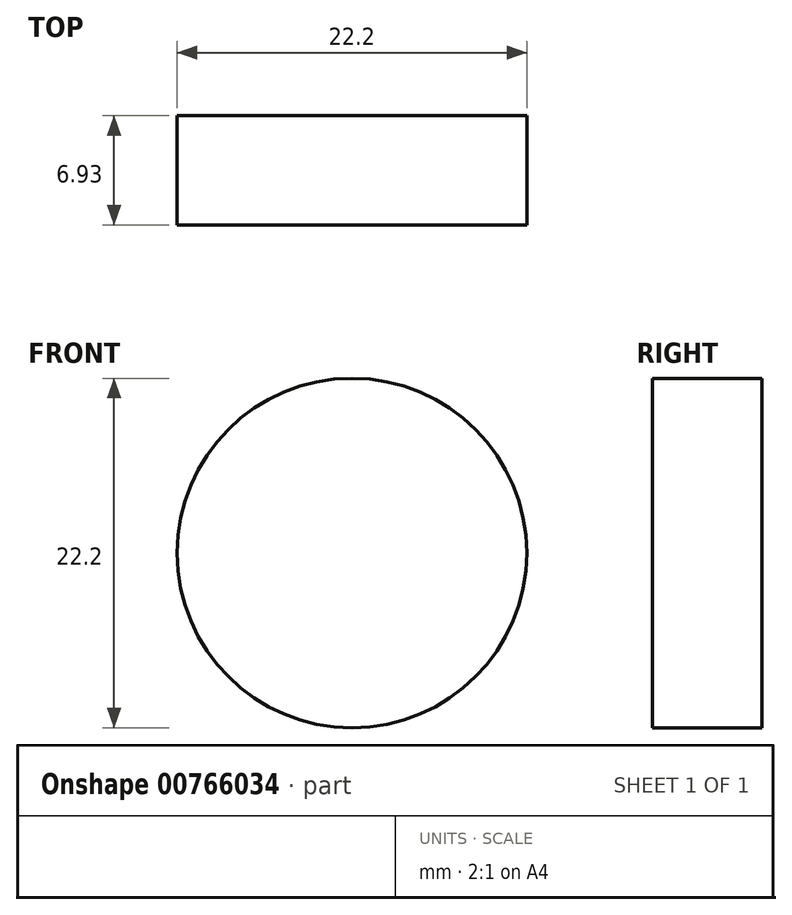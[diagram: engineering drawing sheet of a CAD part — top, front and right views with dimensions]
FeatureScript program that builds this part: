
annotation { "Feature Type Name" : "Feature", "Feature Type Description" : "" }
export const myFeature = defineFeature(function(context is Context, id is Id, definition is map)
    precondition{}
    {
        {
            var Q0;
            Q0=qCreatedBy(makeId("Front.planeOp"),FACE);
            var sketch = newSketch(context, id + "F0", { "sketchPlane" : qUnion([Q0])});
            skCircle(sketch, "E0", {"center": v(0, 0) * mm, "radius": 11.1 * mm});
            skLineSegment(sketch, "E1", {"start": v(-11.1, 0) * mm, "end": v(-11.1, 16.64) * mm});
            skLineSegment(sketch, "E2", {"start": v(-11.1, 16.64) * mm, "end": v(0, 38.02) * mm});
            skLineSegment(sketch, "E3", {"start": v(0, 38.02) * mm, "end": v(20, 50.54) * mm});
            skLineSegment(sketch, "E4", {"start": v(20, 50.54) * mm, "end": v(42.3, 50.54) * mm});
            skLineSegment(sketch, "E5", {"start": v(-22.67, 0) * mm, "end": v(-22.67, 16.34) * mm});
            skLineSegment(sketch, "E6", {"start": v(-22.67, 16.34) * mm, "end": v(-11.1, 41.99) * mm});
            skLineSegment(sketch, "E7", {"start": v(-11.1, 41.99) * mm, "end": v(14.9, 56.65) * mm});
            skLineSegment(sketch, "E8", {"start": v(14.9, 56.65) * mm, "end": v(43.4, 56.65) * mm});
            skSolve(sketch);
        }
        {
            var Q0;
            Q0=makeQuery(id+"F0.imprint","IMPRINT",FACE,{"disambiguationData":[TD([[makeQuery(id+"F0.imprint","IMPRINT",EDGE,{"derivedFrom":sQuery(id+"F0.wireOp",EDGE,"E0")}),1.0]])]});
            extrude(context, id + "F1", {"entities" : qUnion([Q0]), "depth" : 6.93 * mm, "offsetDistance" : 25.4 * mm});
        }
    });
